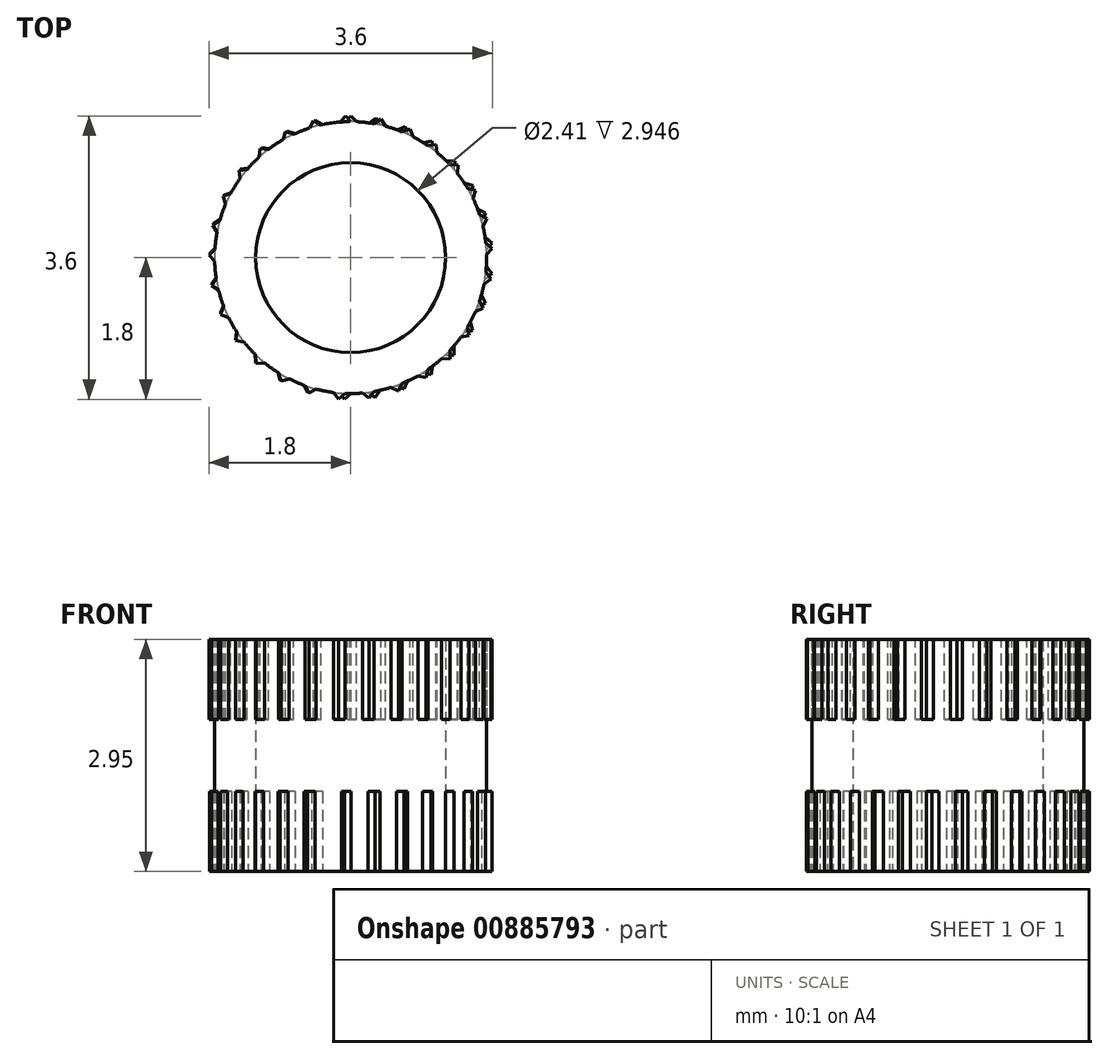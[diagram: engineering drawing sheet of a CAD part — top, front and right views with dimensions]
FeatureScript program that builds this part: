
annotation { "Feature Type Name" : "Feature", "Feature Type Description" : "" }
export const myFeature = defineFeature(function(context is Context, id is Id, definition is map)
    precondition{}
    {
        {
            var Q0;
            Q0=qCreatedBy(makeId("Top.planeOp"),FACE);
            var sketch = newSketch(context, id + "F0", { "sketchPlane" : qUnion([Q0])});
            skCircle(sketch, "E0", {"center": v(0, 0) * mm, "radius": 1.2 * mm});
            skCircle(sketch, "E1", {"center": v(0, 0) * mm, "radius": 1.73 * mm});
            skSolve(sketch);
        }
        {
            var Q0;
            Q0 = qSketchRegion(id + "F0", true);
            extrude(context, id + "F1", {"entities" : qUnion([Q0]), "depth" : 2.95 * mm, "offsetDistance" : 25.4 * mm});
        }
        {
            var Q0;
            Q0=makeQuery(id+"F1.opExtrude","CAP_FACE",FACE,{"disambiguationData":[OSD([sQuery(id+"F0.wireOp",EDGE,"E0"),sQuery(id+"F0.wireOp",EDGE,"E1")])],"isStart":false});
            var sketch = newSketch(context, id + "F2", { "sketchPlane" : qUnion([Q0])});
            skLineSegment(sketch, "E2.bottom", {"start": v(-0.24, 1.56) * mm, "end": v(-0.01, 1.33) * mm});
            skLineSegment(sketch, "E2.top", {"start": v(0, 1.8) * mm, "end": v(0.23, 1.57) * mm});
            skLineSegment(sketch, "E2.left", {"start": v(-0.24, 1.56) * mm, "end": v(0, 1.8) * mm});
            skLineSegment(sketch, "E2.right", {"start": v(-0.01, 1.33) * mm, "end": v(0.23, 1.57) * mm});
            skLineSegment(sketch, "E3.1.0", {"start": v(0.1, 1.57) * mm, "end": v(0.39, 1.76) * mm});
            skLineSegment(sketch, "E3.1.1", {"start": v(0.1, 1.57) * mm, "end": v(0.27, 1.3) * mm});
            skLineSegment(sketch, "E3.1.2", {"start": v(0.39, 1.76) * mm, "end": v(0.56, 1.49) * mm});
            skLineSegment(sketch, "E3.1.3", {"start": v(0.27, 1.3) * mm, "end": v(0.56, 1.49) * mm});
            skLineSegment(sketch, "E3.2.0", {"start": v(0.43, 1.52) * mm, "end": v(0.75, 1.64) * mm});
            skLineSegment(sketch, "E3.2.1", {"start": v(0.43, 1.52) * mm, "end": v(0.55, 1.22) * mm});
            skLineSegment(sketch, "E3.2.2", {"start": v(0.75, 1.64) * mm, "end": v(0.86, 1.34) * mm});
            skLineSegment(sketch, "E3.2.3", {"start": v(0.55, 1.22) * mm, "end": v(0.86, 1.34) * mm});
            skLineSegment(sketch, "E3.3.0", {"start": v(0.75, 1.39) * mm, "end": v(1.08, 1.44) * mm});
            skLineSegment(sketch, "E3.3.1", {"start": v(0.75, 1.39) * mm, "end": v(0.8, 1.07) * mm});
            skLineSegment(sketch, "E3.3.2", {"start": v(1.08, 1.44) * mm, "end": v(1.13, 1.12) * mm});
            skLineSegment(sketch, "E3.3.3", {"start": v(0.8, 1.07) * mm, "end": v(1.13, 1.12) * mm});
            skLineSegment(sketch, "E3.4.0", {"start": v(1.03, 1.2) * mm, "end": v(1.37, 1.17) * mm});
            skLineSegment(sketch, "E3.4.1", {"start": v(1.03, 1.2) * mm, "end": v(1, 0.88) * mm});
            skLineSegment(sketch, "E3.4.2", {"start": v(1.37, 1.17) * mm, "end": v(1.34, 0.85) * mm});
            skLineSegment(sketch, "E3.4.3", {"start": v(1, 0.88) * mm, "end": v(1.34, 0.85) * mm});
            skLineSegment(sketch, "E3.5.0", {"start": v(1.26, 0.95) * mm, "end": v(1.58, 0.85) * mm});
            skLineSegment(sketch, "E3.5.1", {"start": v(1.26, 0.95) * mm, "end": v(1.17, 0.64) * mm});
            skLineSegment(sketch, "E3.5.2", {"start": v(1.58, 0.85) * mm, "end": v(1.5, 0.55) * mm});
            skLineSegment(sketch, "E3.5.3", {"start": v(1.17, 0.64) * mm, "end": v(1.5, 0.55) * mm});
            skLineSegment(sketch, "E3.6.0", {"start": v(1.43, 0.66) * mm, "end": v(1.73, 0.5) * mm});
            skLineSegment(sketch, "E3.6.1", {"start": v(1.43, 0.66) * mm, "end": v(1.28, 0.38) * mm});
            skLineSegment(sketch, "E3.6.2", {"start": v(1.73, 0.5) * mm, "end": v(1.58, 0.22) * mm});
            skLineSegment(sketch, "E3.6.3", {"start": v(1.28, 0.38) * mm, "end": v(1.58, 0.22) * mm});
            skLineSegment(sketch, "E3.7.0", {"start": v(1.54, 0.34) * mm, "end": v(1.8, 0.12) * mm});
            skLineSegment(sketch, "E3.7.1", {"start": v(1.54, 0.34) * mm, "end": v(1.33, 0.1) * mm});
            skLineSegment(sketch, "E3.7.2", {"start": v(1.8, 0.12) * mm, "end": v(1.59, -0.12) * mm});
            skLineSegment(sketch, "E3.7.3", {"start": v(1.33, 0.1) * mm, "end": v(1.59, -0.12) * mm});
            skLineSegment(sketch, "E3.8.0", {"start": v(1.58, 0) * mm, "end": v(1.78, -0.27) * mm});
            skLineSegment(sketch, "E3.8.1", {"start": v(1.58, 0) * mm, "end": v(1.32, -0.19) * mm});
            skLineSegment(sketch, "E3.8.2", {"start": v(1.78, -0.27) * mm, "end": v(1.52, -0.46) * mm});
            skLineSegment(sketch, "E3.8.3", {"start": v(1.32, -0.19) * mm, "end": v(1.52, -0.46) * mm});
            skLineSegment(sketch, "E3.9.0", {"start": v(1.54, -0.33) * mm, "end": v(1.68, -0.64) * mm});
            skLineSegment(sketch, "E3.9.1", {"start": v(1.54, -0.33) * mm, "end": v(1.25, -0.46) * mm});
            skLineSegment(sketch, "E3.9.2", {"start": v(1.68, -0.64) * mm, "end": v(1.39, -0.77) * mm});
            skLineSegment(sketch, "E3.9.3", {"start": v(1.25, -0.46) * mm, "end": v(1.39, -0.77) * mm});
            skLineSegment(sketch, "E3.10.0", {"start": v(1.44, -0.65) * mm, "end": v(1.5, -0.99) * mm});
            skLineSegment(sketch, "E3.10.1", {"start": v(1.44, -0.65) * mm, "end": v(1.12, -0.72) * mm});
            skLineSegment(sketch, "E3.10.2", {"start": v(1.5, -0.99) * mm, "end": v(1.2, -1.05) * mm});
            skLineSegment(sketch, "E3.10.3", {"start": v(1.12, -0.72) * mm, "end": v(1.2, -1.05) * mm});
            skLineSegment(sketch, "E3.11.0", {"start": v(1.26, -0.95) * mm, "end": v(1.26, -1.29) * mm});
            skLineSegment(sketch, "E3.11.1", {"start": v(1.26, -0.95) * mm, "end": v(0.94, -0.94) * mm});
            skLineSegment(sketch, "E3.11.2", {"start": v(1.26, -1.29) * mm, "end": v(0.94, -1.28) * mm});
            skLineSegment(sketch, "E3.11.3", {"start": v(0.94, -0.94) * mm, "end": v(0.94, -1.28) * mm});
            skLineSegment(sketch, "E3.12.0", {"start": v(1.03, -1.2) * mm, "end": v(0.96, -1.52) * mm});
            skLineSegment(sketch, "E3.12.1", {"start": v(1.03, -1.2) * mm, "end": v(0.72, -1.12) * mm});
            skLineSegment(sketch, "E3.12.2", {"start": v(0.96, -1.52) * mm, "end": v(0.65, -1.45) * mm});
            skLineSegment(sketch, "E3.12.3", {"start": v(0.72, -1.12) * mm, "end": v(0.65, -1.45) * mm});
            skLineSegment(sketch, "E3.13.0", {"start": v(0.75, -1.39) * mm, "end": v(0.61, -1.7) * mm});
            skLineSegment(sketch, "E3.13.1", {"start": v(0.75, -1.39) * mm, "end": v(0.46, -1.25) * mm});
            skLineSegment(sketch, "E3.13.2", {"start": v(0.61, -1.7) * mm, "end": v(0.32, -1.56) * mm});
            skLineSegment(sketch, "E3.13.3", {"start": v(0.46, -1.25) * mm, "end": v(0.32, -1.56) * mm});
            skLineSegment(sketch, "E3.14.0", {"start": v(0.44, -1.51) * mm, "end": v(0.23, -1.79) * mm});
            skLineSegment(sketch, "E3.14.1", {"start": v(0.44, -1.51) * mm, "end": v(0.19, -1.32) * mm});
            skLineSegment(sketch, "E3.14.2", {"start": v(0.23, -1.79) * mm, "end": v(-0.02, -1.6) * mm});
            skLineSegment(sketch, "E3.14.3", {"start": v(0.19, -1.32) * mm, "end": v(-0.02, -1.6) * mm});
            skLineSegment(sketch, "E3.15.0", {"start": v(0.1, -1.57) * mm, "end": v(-0.15, -1.8) * mm});
            skLineSegment(sketch, "E3.15.1", {"start": v(0.1, -1.57) * mm, "end": v(-0.1, -1.33) * mm});
            skLineSegment(sketch, "E3.15.2", {"start": v(-0.15, -1.8) * mm, "end": v(-0.36, -1.55) * mm});
            skLineSegment(sketch, "E3.15.3", {"start": v(-0.1, -1.33) * mm, "end": v(-0.36, -1.55) * mm});
            skLineSegment(sketch, "E3.16.0", {"start": v(-0.23, -1.56) * mm, "end": v(-0.53, -1.72) * mm});
            skLineSegment(sketch, "E3.16.1", {"start": v(-0.23, -1.56) * mm, "end": v(-0.38, -1.28) * mm});
            skLineSegment(sketch, "E3.16.2", {"start": v(-0.53, -1.72) * mm, "end": v(-0.68, -1.44) * mm});
            skLineSegment(sketch, "E3.16.3", {"start": v(-0.38, -1.28) * mm, "end": v(-0.68, -1.44) * mm});
            skLineSegment(sketch, "E3.17.0", {"start": v(-0.56, -1.48) * mm, "end": v(-0.89, -1.57) * mm});
            skLineSegment(sketch, "E3.17.1", {"start": v(-0.56, -1.48) * mm, "end": v(-0.64, -1.17) * mm});
            skLineSegment(sketch, "E3.17.2", {"start": v(-0.89, -1.57) * mm, "end": v(-0.97, -1.26) * mm});
            skLineSegment(sketch, "E3.17.3", {"start": v(-0.64, -1.17) * mm, "end": v(-0.97, -1.26) * mm});
            skLineSegment(sketch, "E3.18.0", {"start": v(-0.86, -1.32) * mm, "end": v(-1.2, -1.34) * mm});
            skLineSegment(sketch, "E3.18.1", {"start": v(-0.86, -1.32) * mm, "end": v(-0.88, -1) * mm});
            skLineSegment(sketch, "E3.18.2", {"start": v(-1.2, -1.34) * mm, "end": v(-1.22, -1.02) * mm});
            skLineSegment(sketch, "E3.18.3", {"start": v(-0.88, -1) * mm, "end": v(-1.22, -1.02) * mm});
            skLineSegment(sketch, "E3.19.0", {"start": v(-1.12, -1.1) * mm, "end": v(-1.46, -1.06) * mm});
            skLineSegment(sketch, "E3.19.1", {"start": v(-1.12, -1.1) * mm, "end": v(-1.07, -0.8) * mm});
            skLineSegment(sketch, "E3.19.2", {"start": v(-1.46, -1.06) * mm, "end": v(-1.4, -0.74) * mm});
            skLineSegment(sketch, "E3.19.3", {"start": v(-1.07, -0.8) * mm, "end": v(-1.4, -0.74) * mm});
            skLineSegment(sketch, "E3.20.0", {"start": v(-1.33, -0.84) * mm, "end": v(-1.65, -0.72) * mm});
            skLineSegment(sketch, "E3.20.1", {"start": v(-1.33, -0.84) * mm, "end": v(-1.22, -0.55) * mm});
            skLineSegment(sketch, "E3.20.2", {"start": v(-1.65, -0.72) * mm, "end": v(-1.53, -0.42) * mm});
            skLineSegment(sketch, "E3.20.3", {"start": v(-1.22, -0.55) * mm, "end": v(-1.53, -0.42) * mm});
            skLineSegment(sketch, "E3.21.0", {"start": v(-1.48, -0.54) * mm, "end": v(-1.77, -0.35) * mm});
            skLineSegment(sketch, "E3.21.1", {"start": v(-1.48, -0.54) * mm, "end": v(-1.3, -0.27) * mm});
            skLineSegment(sketch, "E3.21.2", {"start": v(-1.77, -0.35) * mm, "end": v(-1.59, -0.09) * mm});
            skLineSegment(sketch, "E3.21.3", {"start": v(-1.3, -0.27) * mm, "end": v(-1.59, -0.09) * mm});
            skLineSegment(sketch, "E3.22.0", {"start": v(-1.56, -0.21) * mm, "end": v(-1.8, 0.03) * mm});
            skLineSegment(sketch, "E3.22.1", {"start": v(-1.56, -0.21) * mm, "end": v(-1.33, 0.01) * mm});
            skLineSegment(sketch, "E3.22.2", {"start": v(-1.8, 0.03) * mm, "end": v(-1.57, 0.25) * mm});
            skLineSegment(sketch, "E3.22.3", {"start": v(-1.33, 0.01) * mm, "end": v(-1.57, 0.25) * mm});
            skLineSegment(sketch, "E3.23.0", {"start": v(-1.57, 0.13) * mm, "end": v(-1.75, 0.42) * mm});
            skLineSegment(sketch, "E3.23.1", {"start": v(-1.57, 0.13) * mm, "end": v(-1.3, 0.3) * mm});
            skLineSegment(sketch, "E3.23.2", {"start": v(-1.75, 0.42) * mm, "end": v(-1.48, 0.58) * mm});
            skLineSegment(sketch, "E3.23.3", {"start": v(-1.3, 0.3) * mm, "end": v(-1.48, 0.58) * mm});
            skLineSegment(sketch, "E3.24.0", {"start": v(-1.5, 0.46) * mm, "end": v(-1.62, 0.78) * mm});
            skLineSegment(sketch, "E3.24.1", {"start": v(-1.5, 0.46) * mm, "end": v(-1.2, 0.56) * mm});
            skLineSegment(sketch, "E3.24.2", {"start": v(-1.62, 0.78) * mm, "end": v(-1.32, 0.89) * mm});
            skLineSegment(sketch, "E3.24.3", {"start": v(-1.2, 0.56) * mm, "end": v(-1.32, 0.89) * mm});
            skLineSegment(sketch, "E3.25.0", {"start": v(-1.38, 0.77) * mm, "end": v(-1.42, 1.1) * mm});
            skLineSegment(sketch, "E3.25.1", {"start": v(-1.38, 0.77) * mm, "end": v(-1.06, 0.8) * mm});
            skLineSegment(sketch, "E3.25.2", {"start": v(-1.42, 1.1) * mm, "end": v(-1.1, 1.15) * mm});
            skLineSegment(sketch, "E3.25.3", {"start": v(-1.06, 0.8) * mm, "end": v(-1.1, 1.15) * mm});
            skLineSegment(sketch, "E3.26.0", {"start": v(-1.18, 1.05) * mm, "end": v(-1.15, 1.38) * mm});
            skLineSegment(sketch, "E3.26.1", {"start": v(-1.18, 1.05) * mm, "end": v(-0.86, 1.02) * mm});
            skLineSegment(sketch, "E3.26.2", {"start": v(-1.15, 1.38) * mm, "end": v(-0.83, 1.36) * mm});
            skLineSegment(sketch, "E3.26.3", {"start": v(-0.86, 1.02) * mm, "end": v(-0.83, 1.36) * mm});
            skLineSegment(sketch, "E3.27.0", {"start": v(-0.93, 1.27) * mm, "end": v(-0.83, 1.6) * mm});
            skLineSegment(sketch, "E3.27.1", {"start": v(-0.93, 1.27) * mm, "end": v(-0.63, 1.18) * mm});
            skLineSegment(sketch, "E3.27.2", {"start": v(-0.83, 1.6) * mm, "end": v(-0.52, 1.5) * mm});
            skLineSegment(sketch, "E3.27.3", {"start": v(-0.63, 1.18) * mm, "end": v(-0.52, 1.5) * mm});
            skLineSegment(sketch, "E3.28.0", {"start": v(-0.64, 1.44) * mm, "end": v(-0.47, 1.74) * mm});
            skLineSegment(sketch, "E3.28.1", {"start": v(-0.64, 1.44) * mm, "end": v(-0.36, 1.28) * mm});
            skLineSegment(sketch, "E3.28.2", {"start": v(-0.47, 1.74) * mm, "end": v(-0.2, 1.58) * mm});
            skLineSegment(sketch, "E3.28.3", {"start": v(-0.36, 1.28) * mm, "end": v(-0.2, 1.58) * mm});
            skLineSegment(sketch, "E3.29.0", {"start": v(-0.32, 1.55) * mm, "end": v(-0.09, 1.8) * mm});
            skLineSegment(sketch, "E3.29.1", {"start": v(-0.32, 1.55) * mm, "end": v(-0.08, 1.33) * mm});
            skLineSegment(sketch, "E3.29.2", {"start": v(-0.09, 1.8) * mm, "end": v(0.15, 1.58) * mm});
            skLineSegment(sketch, "E3.29.3", {"start": v(-0.08, 1.33) * mm, "end": v(0.15, 1.58) * mm});
            skPoint(sketch, "E3.center", {"position": v(0, 0) * mm});
            skLineSegment(sketch, "E3.anchor1", {"start": v(0, 0) * mm, "end": v(-0.01, 1.33) * mm, "construction": true});
            skLineSegment(sketch, "E3.anchor2", {"start": v(0, 0) * mm, "end": v(-0.08, 1.33) * mm, "construction": true});
            skSolve(sketch);
        }
        {
            var Q0;
            {var subQ0=sQuery(id+"F2.wireOp",EDGE,"E3.25.2");var subQ1=sQuery(id+"F2.wireOp",EDGE,"E3.25.0");var subQ2=makeQuery(id+"F2.imprint","INTERSECT",VERTEX,{"derivedFrom":[subQ1,subQ0]});Q0=makeQuery(id+"F2.imprint","IMPRINT",FACE,{"disambiguationData":[TD([[makeQuery(id+"F2.imprint","IMPRINT",EDGE,{"disambiguationData":[TD([[subQ2,1.0]])],"derivedFrom":subQ1}),-1.0]])]});}
            var Q1;
            {var subQ0=sQuery(id+"F2.wireOp",EDGE,"E3.26.2");var subQ1=sQuery(id+"F2.wireOp",EDGE,"E3.26.0");var subQ2=makeQuery(id+"F2.imprint","INTERSECT",VERTEX,{"derivedFrom":[subQ1,subQ0]});Q1=makeQuery(id+"F2.imprint","IMPRINT",FACE,{"disambiguationData":[TD([[makeQuery(id+"F2.imprint","IMPRINT",EDGE,{"disambiguationData":[TD([[subQ2,1.0]])],"derivedFrom":subQ1}),-1.0]])]});}
            var Q2;
            {var subQ0=sQuery(id+"F2.wireOp",EDGE,"E3.27.2");var subQ1=sQuery(id+"F2.wireOp",EDGE,"E3.27.0");var subQ2=makeQuery(id+"F2.imprint","INTERSECT",VERTEX,{"derivedFrom":[subQ1,subQ0]});Q2=makeQuery(id+"F2.imprint","IMPRINT",FACE,{"disambiguationData":[TD([[makeQuery(id+"F2.imprint","IMPRINT",EDGE,{"disambiguationData":[TD([[subQ2,1.0]])],"derivedFrom":subQ1}),-1.0]])]});}
            var Q3;
            {var subQ0=sQuery(id+"F2.wireOp",EDGE,"E3.28.2");var subQ1=sQuery(id+"F2.wireOp",EDGE,"E3.28.0");var subQ2=makeQuery(id+"F2.imprint","INTERSECT",VERTEX,{"derivedFrom":[subQ1,subQ0]});Q3=makeQuery(id+"F2.imprint","IMPRINT",FACE,{"disambiguationData":[TD([[makeQuery(id+"F2.imprint","IMPRINT",EDGE,{"disambiguationData":[TD([[subQ2,1.0]])],"derivedFrom":subQ1}),-1.0]])]});}
            var Q4;
            {var subQ0=sQuery(id+"F2.wireOp",EDGE,"E2.left");var subQ1=sQuery(id+"F2.wireOp",EDGE,"E2.top");var subQ2=makeQuery(id+"F2.imprint","INTERSECT",VERTEX,{"derivedFrom":[subQ1,subQ0]});Q4=makeQuery(id+"F2.imprint","IMPRINT",FACE,{"disambiguationData":[TD([[makeQuery(id+"F2.imprint","IMPRINT",EDGE,{"disambiguationData":[TD([[subQ2,-1.0]])],"derivedFrom":subQ1}),-1.0]])]});}
            var Q5;
            {var subQ0=sQuery(id+"F2.wireOp",EDGE,"E3.1.2");var subQ1=sQuery(id+"F2.wireOp",EDGE,"E3.1.0");var subQ2=makeQuery(id+"F2.imprint","INTERSECT",VERTEX,{"derivedFrom":[subQ1,subQ0]});Q5=makeQuery(id+"F2.imprint","IMPRINT",FACE,{"disambiguationData":[TD([[makeQuery(id+"F2.imprint","IMPRINT",EDGE,{"disambiguationData":[TD([[subQ2,1.0]])],"derivedFrom":subQ1}),-1.0]])]});}
            var Q6;
            {var subQ0=sQuery(id+"F2.wireOp",EDGE,"E3.2.2");var subQ1=sQuery(id+"F2.wireOp",EDGE,"E3.2.0");var subQ2=makeQuery(id+"F2.imprint","INTERSECT",VERTEX,{"derivedFrom":[subQ1,subQ0]});Q6=makeQuery(id+"F2.imprint","IMPRINT",FACE,{"disambiguationData":[TD([[makeQuery(id+"F2.imprint","IMPRINT",EDGE,{"disambiguationData":[TD([[subQ2,1.0]])],"derivedFrom":subQ1}),-1.0]])]});}
            var Q7;
            {var subQ0=sQuery(id+"F2.wireOp",EDGE,"E3.4.2");var subQ1=sQuery(id+"F2.wireOp",EDGE,"E3.4.0");var subQ2=makeQuery(id+"F2.imprint","INTERSECT",VERTEX,{"derivedFrom":[subQ1,subQ0]});Q7=makeQuery(id+"F2.imprint","IMPRINT",FACE,{"disambiguationData":[TD([[makeQuery(id+"F2.imprint","IMPRINT",EDGE,{"disambiguationData":[TD([[subQ2,1.0]])],"derivedFrom":subQ1}),-1.0]])]});}
            var Q8;
            {var subQ0=sQuery(id+"F2.wireOp",EDGE,"E3.5.2");var subQ1=sQuery(id+"F2.wireOp",EDGE,"E3.5.0");var subQ2=makeQuery(id+"F2.imprint","INTERSECT",VERTEX,{"derivedFrom":[subQ1,subQ0]});Q8=makeQuery(id+"F2.imprint","IMPRINT",FACE,{"disambiguationData":[TD([[makeQuery(id+"F2.imprint","IMPRINT",EDGE,{"disambiguationData":[TD([[subQ2,1.0]])],"derivedFrom":subQ1}),-1.0]])]});}
            var Q9;
            {var subQ0=sQuery(id+"F2.wireOp",EDGE,"E3.6.2");var subQ1=sQuery(id+"F2.wireOp",EDGE,"E3.6.0");var subQ2=makeQuery(id+"F2.imprint","INTERSECT",VERTEX,{"derivedFrom":[subQ1,subQ0]});Q9=makeQuery(id+"F2.imprint","IMPRINT",FACE,{"disambiguationData":[TD([[makeQuery(id+"F2.imprint","IMPRINT",EDGE,{"disambiguationData":[TD([[subQ2,1.0]])],"derivedFrom":subQ1}),-1.0]])]});}
            var Q10;
            {var subQ0=sQuery(id+"F2.wireOp",EDGE,"E3.7.2");var subQ1=sQuery(id+"F2.wireOp",EDGE,"E3.7.0");var subQ2=makeQuery(id+"F2.imprint","INTERSECT",VERTEX,{"derivedFrom":[subQ1,subQ0]});Q10=makeQuery(id+"F2.imprint","IMPRINT",FACE,{"disambiguationData":[TD([[makeQuery(id+"F2.imprint","IMPRINT",EDGE,{"disambiguationData":[TD([[subQ2,1.0]])],"derivedFrom":subQ1}),-1.0]])]});}
            var Q11;
            {var subQ0=sQuery(id+"F2.wireOp",EDGE,"E3.8.2");var subQ1=sQuery(id+"F2.wireOp",EDGE,"E3.8.0");var subQ2=makeQuery(id+"F2.imprint","INTERSECT",VERTEX,{"derivedFrom":[subQ1,subQ0]});Q11=makeQuery(id+"F2.imprint","IMPRINT",FACE,{"disambiguationData":[TD([[makeQuery(id+"F2.imprint","IMPRINT",EDGE,{"disambiguationData":[TD([[subQ2,1.0]])],"derivedFrom":subQ1}),-1.0]])]});}
            var Q12;
            {var subQ0=sQuery(id+"F2.wireOp",EDGE,"E3.23.2");var subQ1=sQuery(id+"F2.wireOp",EDGE,"E3.23.0");var subQ2=makeQuery(id+"F2.imprint","INTERSECT",VERTEX,{"derivedFrom":[subQ1,subQ0]});Q12=makeQuery(id+"F2.imprint","IMPRINT",FACE,{"disambiguationData":[TD([[makeQuery(id+"F2.imprint","IMPRINT",EDGE,{"disambiguationData":[TD([[subQ2,1.0]])],"derivedFrom":subQ1}),-1.0]])]});}
            var Q13;
            {var subQ0=sQuery(id+"F2.wireOp",EDGE,"E3.21.2");var subQ1=sQuery(id+"F2.wireOp",EDGE,"E3.21.0");var subQ2=makeQuery(id+"F2.imprint","INTERSECT",VERTEX,{"derivedFrom":[subQ1,subQ0]});Q13=makeQuery(id+"F2.imprint","IMPRINT",FACE,{"disambiguationData":[TD([[makeQuery(id+"F2.imprint","IMPRINT",EDGE,{"disambiguationData":[TD([[subQ2,1.0]])],"derivedFrom":subQ1}),-1.0]])]});}
            var Q14;
            {var subQ0=sQuery(id+"F2.wireOp",EDGE,"E3.20.2");var subQ1=sQuery(id+"F2.wireOp",EDGE,"E3.20.0");var subQ2=makeQuery(id+"F2.imprint","INTERSECT",VERTEX,{"derivedFrom":[subQ1,subQ0]});Q14=makeQuery(id+"F2.imprint","IMPRINT",FACE,{"disambiguationData":[TD([[makeQuery(id+"F2.imprint","IMPRINT",EDGE,{"disambiguationData":[TD([[subQ2,1.0]])],"derivedFrom":subQ1}),-1.0]])]});}
            var Q15;
            {var subQ0=sQuery(id+"F2.wireOp",EDGE,"E3.19.2");var subQ1=sQuery(id+"F2.wireOp",EDGE,"E3.19.0");var subQ2=makeQuery(id+"F2.imprint","INTERSECT",VERTEX,{"derivedFrom":[subQ1,subQ0]});Q15=makeQuery(id+"F2.imprint","IMPRINT",FACE,{"disambiguationData":[TD([[makeQuery(id+"F2.imprint","IMPRINT",EDGE,{"disambiguationData":[TD([[subQ2,1.0]])],"derivedFrom":subQ1}),-1.0]])]});}
            var Q16;
            {var subQ0=sQuery(id+"F2.wireOp",EDGE,"E3.18.2");var subQ1=sQuery(id+"F2.wireOp",EDGE,"E3.18.0");var subQ2=makeQuery(id+"F2.imprint","INTERSECT",VERTEX,{"derivedFrom":[subQ1,subQ0]});Q16=makeQuery(id+"F2.imprint","IMPRINT",FACE,{"disambiguationData":[TD([[makeQuery(id+"F2.imprint","IMPRINT",EDGE,{"disambiguationData":[TD([[subQ2,1.0]])],"derivedFrom":subQ1}),-1.0]])]});}
            var Q17;
            {var subQ0=sQuery(id+"F2.wireOp",EDGE,"E3.17.2");var subQ1=sQuery(id+"F2.wireOp",EDGE,"E3.17.0");var subQ2=makeQuery(id+"F2.imprint","INTERSECT",VERTEX,{"derivedFrom":[subQ1,subQ0]});Q17=makeQuery(id+"F2.imprint","IMPRINT",FACE,{"disambiguationData":[TD([[makeQuery(id+"F2.imprint","IMPRINT",EDGE,{"disambiguationData":[TD([[subQ2,1.0]])],"derivedFrom":subQ1}),-1.0]])]});}
            var Q18;
            {var subQ0=sQuery(id+"F2.wireOp",EDGE,"E3.16.2");var subQ1=sQuery(id+"F2.wireOp",EDGE,"E3.16.0");var subQ2=makeQuery(id+"F2.imprint","INTERSECT",VERTEX,{"derivedFrom":[subQ1,subQ0]});Q18=makeQuery(id+"F2.imprint","IMPRINT",FACE,{"disambiguationData":[TD([[makeQuery(id+"F2.imprint","IMPRINT",EDGE,{"disambiguationData":[TD([[subQ2,1.0]])],"derivedFrom":subQ1}),-1.0]])]});}
            var Q19;
            {var subQ0=sQuery(id+"F2.wireOp",EDGE,"E3.15.2");var subQ1=sQuery(id+"F2.wireOp",EDGE,"E3.15.0");var subQ2=makeQuery(id+"F2.imprint","INTERSECT",VERTEX,{"derivedFrom":[subQ1,subQ0]});Q19=makeQuery(id+"F2.imprint","IMPRINT",FACE,{"disambiguationData":[TD([[makeQuery(id+"F2.imprint","IMPRINT",EDGE,{"disambiguationData":[TD([[subQ2,1.0]])],"derivedFrom":subQ1}),-1.0]])]});}
            var Q20;
            {var subQ0=sQuery(id+"F2.wireOp",EDGE,"E3.14.2");var subQ1=sQuery(id+"F2.wireOp",EDGE,"E3.14.0");var subQ2=makeQuery(id+"F2.imprint","INTERSECT",VERTEX,{"derivedFrom":[subQ1,subQ0]});Q20=makeQuery(id+"F2.imprint","IMPRINT",FACE,{"disambiguationData":[TD([[makeQuery(id+"F2.imprint","IMPRINT",EDGE,{"disambiguationData":[TD([[subQ2,1.0]])],"derivedFrom":subQ1}),-1.0]])]});}
            var Q21;
            {var subQ0=sQuery(id+"F2.wireOp",EDGE,"E3.13.2");var subQ1=sQuery(id+"F2.wireOp",EDGE,"E3.13.0");var subQ2=makeQuery(id+"F2.imprint","INTERSECT",VERTEX,{"derivedFrom":[subQ1,subQ0]});Q21=makeQuery(id+"F2.imprint","IMPRINT",FACE,{"disambiguationData":[TD([[makeQuery(id+"F2.imprint","IMPRINT",EDGE,{"disambiguationData":[TD([[subQ2,1.0]])],"derivedFrom":subQ1}),-1.0]])]});}
            var Q22;
            {var subQ0=sQuery(id+"F2.wireOp",EDGE,"E3.12.2");var subQ1=sQuery(id+"F2.wireOp",EDGE,"E3.12.0");var subQ2=makeQuery(id+"F2.imprint","INTERSECT",VERTEX,{"derivedFrom":[subQ1,subQ0]});Q22=makeQuery(id+"F2.imprint","IMPRINT",FACE,{"disambiguationData":[TD([[makeQuery(id+"F2.imprint","IMPRINT",EDGE,{"disambiguationData":[TD([[subQ2,1.0]])],"derivedFrom":subQ1}),-1.0]])]});}
            var Q23;
            {var subQ0=sQuery(id+"F2.wireOp",EDGE,"E3.11.2");var subQ1=sQuery(id+"F2.wireOp",EDGE,"E3.11.0");var subQ2=makeQuery(id+"F2.imprint","INTERSECT",VERTEX,{"derivedFrom":[subQ1,subQ0]});Q23=makeQuery(id+"F2.imprint","IMPRINT",FACE,{"disambiguationData":[TD([[makeQuery(id+"F2.imprint","IMPRINT",EDGE,{"disambiguationData":[TD([[subQ2,1.0]])],"derivedFrom":subQ1}),-1.0]])]});}
            var Q24;
            {var subQ0=sQuery(id+"F2.wireOp",EDGE,"E3.10.2");var subQ1=sQuery(id+"F2.wireOp",EDGE,"E3.10.0");var subQ2=makeQuery(id+"F2.imprint","INTERSECT",VERTEX,{"derivedFrom":[subQ1,subQ0]});Q24=makeQuery(id+"F2.imprint","IMPRINT",FACE,{"disambiguationData":[TD([[makeQuery(id+"F2.imprint","IMPRINT",EDGE,{"disambiguationData":[TD([[subQ2,1.0]])],"derivedFrom":subQ1}),-1.0]])]});}
            var Q25;
            {var subQ0=sQuery(id+"F2.wireOp",EDGE,"E3.9.2");var subQ1=sQuery(id+"F2.wireOp",EDGE,"E3.9.0");var subQ2=makeQuery(id+"F2.imprint","INTERSECT",VERTEX,{"derivedFrom":[subQ1,subQ0]});Q25=makeQuery(id+"F2.imprint","IMPRINT",FACE,{"disambiguationData":[TD([[makeQuery(id+"F2.imprint","IMPRINT",EDGE,{"disambiguationData":[TD([[subQ2,1.0]])],"derivedFrom":subQ1}),-1.0]])]});}
            var Q26;
            {var subQ0=sQuery(id+"F2.wireOp",EDGE,"E3.3.2");var subQ1=sQuery(id+"F2.wireOp",EDGE,"E3.3.0");var subQ2=makeQuery(id+"F2.imprint","INTERSECT",VERTEX,{"derivedFrom":[subQ1,subQ0]});Q26=makeQuery(id+"F2.imprint","IMPRINT",FACE,{"disambiguationData":[TD([[makeQuery(id+"F2.imprint","IMPRINT",EDGE,{"disambiguationData":[TD([[subQ2,1.0]])],"derivedFrom":subQ1}),-1.0]])]});}
            var Q27;
            {var subQ0=sQuery(id+"F2.wireOp",EDGE,"E3.24.2");var subQ1=sQuery(id+"F2.wireOp",EDGE,"E3.24.0");var subQ2=makeQuery(id+"F2.imprint","INTERSECT",VERTEX,{"derivedFrom":[subQ1,subQ0]});Q27=makeQuery(id+"F2.imprint","IMPRINT",FACE,{"disambiguationData":[TD([[makeQuery(id+"F2.imprint","IMPRINT",EDGE,{"disambiguationData":[TD([[subQ2,1.0]])],"derivedFrom":subQ1}),-1.0]])]});}
            var Q28;
            {var subQ0=sQuery(id+"F2.wireOp",EDGE,"E3.22.2");var subQ1=sQuery(id+"F2.wireOp",EDGE,"E3.22.0");var subQ2=makeQuery(id+"F2.imprint","INTERSECT",VERTEX,{"derivedFrom":[subQ1,subQ0]});Q28=makeQuery(id+"F2.imprint","IMPRINT",FACE,{"disambiguationData":[TD([[makeQuery(id+"F2.imprint","IMPRINT",EDGE,{"disambiguationData":[TD([[subQ2,1.0]])],"derivedFrom":subQ1}),-1.0]])]});}
            extrude(context, id + "F3", {"entities" : qUnion([Q0, Q1, Q2, Q3, Q4, Q5, Q6, Q7, Q8, Q9, Q10, Q11, Q12, Q13, Q14, Q15, Q16, Q17, Q18, Q19, Q20, Q21, Q22, Q23, Q24, Q25, Q26, Q27, Q28]), "operationType" : NewBodyOperationType.ADD, "oppositeDirection" : true, "depth" : 1.02 * mm, "offsetDistance" : 25.4 * mm});
        }
        {
            var Q0;
            Q0=makeQuery(id+"F1.opExtrude","CAP_FACE",FACE,{"disambiguationData":[OSD([sQuery(id+"F0.wireOp",EDGE,"E0"),sQuery(id+"F0.wireOp",EDGE,"E1")])],"isStart":true});
            var sketch = newSketch(context, id + "F4", { "sketchPlane" : qUnion([Q0])});
            skLineSegment(sketch, "E4.bottom", {"start": v(-0.3, 1.55) * mm, "end": v(-0.07, 1.33) * mm});
            skLineSegment(sketch, "E4.top", {"start": v(-0.08, 1.8) * mm, "end": v(0.16, 1.58) * mm});
            skLineSegment(sketch, "E4.left", {"start": v(-0.3, 1.55) * mm, "end": v(-0.08, 1.8) * mm});
            skLineSegment(sketch, "E4.right", {"start": v(-0.07, 1.33) * mm, "end": v(0.16, 1.58) * mm});
            skLineSegment(sketch, "E5.1.0", {"start": v(0.03, 1.58) * mm, "end": v(0.3, 1.77) * mm});
            skLineSegment(sketch, "E5.1.1", {"start": v(0.03, 1.58) * mm, "end": v(0.22, 1.32) * mm});
            skLineSegment(sketch, "E5.1.2", {"start": v(0.3, 1.77) * mm, "end": v(0.5, 1.51) * mm});
            skLineSegment(sketch, "E5.1.3", {"start": v(0.22, 1.32) * mm, "end": v(0.5, 1.51) * mm});
            skLineSegment(sketch, "E5.2.0", {"start": v(0.37, 1.54) * mm, "end": v(0.68, 1.67) * mm});
            skLineSegment(sketch, "E5.2.1", {"start": v(0.37, 1.54) * mm, "end": v(0.5, 1.24) * mm});
            skLineSegment(sketch, "E5.2.2", {"start": v(0.68, 1.67) * mm, "end": v(0.8, 1.37) * mm});
            skLineSegment(sketch, "E5.2.3", {"start": v(0.5, 1.24) * mm, "end": v(0.8, 1.37) * mm});
            skLineSegment(sketch, "E5.3.0", {"start": v(0.69, 1.42) * mm, "end": v(1.02, 1.49) * mm});
            skLineSegment(sketch, "E5.3.1", {"start": v(0.69, 1.42) * mm, "end": v(0.75, 1.1) * mm});
            skLineSegment(sketch, "E5.3.2", {"start": v(1.02, 1.49) * mm, "end": v(1.08, 1.17) * mm});
            skLineSegment(sketch, "E5.3.3", {"start": v(0.75, 1.1) * mm, "end": v(1.08, 1.17) * mm});
            skLineSegment(sketch, "E5.4.0", {"start": v(0.97, 1.24) * mm, "end": v(1.32, 1.24) * mm});
            skLineSegment(sketch, "E5.4.1", {"start": v(0.97, 1.24) * mm, "end": v(0.97, 0.92) * mm});
            skLineSegment(sketch, "E5.4.2", {"start": v(1.32, 1.24) * mm, "end": v(1.3, 0.92) * mm});
            skLineSegment(sketch, "E5.4.3", {"start": v(0.97, 0.92) * mm, "end": v(1.3, 0.92) * mm});
            skLineSegment(sketch, "E5.5.0", {"start": v(1.22, 1) * mm, "end": v(1.55, 0.93) * mm});
            skLineSegment(sketch, "E5.5.1", {"start": v(1.22, 1) * mm, "end": v(1.14, 0.7) * mm});
            skLineSegment(sketch, "E5.5.2", {"start": v(1.55, 0.93) * mm, "end": v(1.47, 0.62) * mm});
            skLineSegment(sketch, "E5.5.3", {"start": v(1.14, 0.7) * mm, "end": v(1.47, 0.62) * mm});
            skLineSegment(sketch, "E5.6.0", {"start": v(1.4, 0.73) * mm, "end": v(1.71, 0.58) * mm});
            skLineSegment(sketch, "E5.6.1", {"start": v(1.4, 0.73) * mm, "end": v(1.26, 0.44) * mm});
            skLineSegment(sketch, "E5.6.2", {"start": v(1.71, 0.58) * mm, "end": v(1.57, 0.3) * mm});
            skLineSegment(sketch, "E5.6.3", {"start": v(1.26, 0.44) * mm, "end": v(1.57, 0.3) * mm});
            skLineSegment(sketch, "E5.7.0", {"start": v(1.53, 0.41) * mm, "end": v(1.8, 0.2) * mm});
            skLineSegment(sketch, "E5.7.1", {"start": v(1.53, 0.41) * mm, "end": v(1.33, 0.16) * mm});
            skLineSegment(sketch, "E5.7.2", {"start": v(1.8, 0.2) * mm, "end": v(1.6, -0.05) * mm});
            skLineSegment(sketch, "E5.7.3", {"start": v(1.33, 0.16) * mm, "end": v(1.6, -0.05) * mm});
            skLineSegment(sketch, "E5.8.0", {"start": v(1.58, 0.08) * mm, "end": v(1.8, -0.19) * mm});
            skLineSegment(sketch, "E5.8.1", {"start": v(1.58, 0.08) * mm, "end": v(1.33, -0.12) * mm});
            skLineSegment(sketch, "E5.8.2", {"start": v(1.8, -0.19) * mm, "end": v(1.55, -0.39) * mm});
            skLineSegment(sketch, "E5.8.3", {"start": v(1.33, -0.12) * mm, "end": v(1.55, -0.39) * mm});
            skLineSegment(sketch, "E5.9.0", {"start": v(1.56, -0.26) * mm, "end": v(1.72, -0.56) * mm});
            skLineSegment(sketch, "E5.9.1", {"start": v(1.56, -0.26) * mm, "end": v(1.28, -0.4) * mm});
            skLineSegment(sketch, "E5.9.2", {"start": v(1.72, -0.56) * mm, "end": v(1.43, -0.7) * mm});
            skLineSegment(sketch, "E5.9.3", {"start": v(1.28, -0.4) * mm, "end": v(1.43, -0.7) * mm});
            skLineSegment(sketch, "E5.10.0", {"start": v(1.47, -0.59) * mm, "end": v(1.56, -0.92) * mm});
            skLineSegment(sketch, "E5.10.1", {"start": v(1.47, -0.59) * mm, "end": v(1.16, -0.67) * mm});
            skLineSegment(sketch, "E5.10.2", {"start": v(1.56, -0.92) * mm, "end": v(1.25, -1) * mm});
            skLineSegment(sketch, "E5.10.3", {"start": v(1.16, -0.67) * mm, "end": v(1.25, -1) * mm});
            skLineSegment(sketch, "E5.11.0", {"start": v(1.31, -0.88) * mm, "end": v(1.32, -1.23) * mm});
            skLineSegment(sketch, "E5.11.1", {"start": v(1.31, -0.88) * mm, "end": v(1, -0.9) * mm});
            skLineSegment(sketch, "E5.11.2", {"start": v(1.32, -1.23) * mm, "end": v(1, -1.24) * mm});
            skLineSegment(sketch, "E5.11.3", {"start": v(1, -0.9) * mm, "end": v(1, -1.24) * mm});
            skLineSegment(sketch, "E5.12.0", {"start": v(1.1, -1.14) * mm, "end": v(1.03, -1.48) * mm});
            skLineSegment(sketch, "E5.12.1", {"start": v(1.1, -1.14) * mm, "end": v(0.78, -1.09) * mm});
            skLineSegment(sketch, "E5.12.2", {"start": v(1.03, -1.48) * mm, "end": v(0.72, -1.42) * mm});
            skLineSegment(sketch, "E5.12.3", {"start": v(0.78, -1.09) * mm, "end": v(0.72, -1.42) * mm});
            skLineSegment(sketch, "E5.13.0", {"start": v(0.82, -1.35) * mm, "end": v(0.7, -1.66) * mm});
            skLineSegment(sketch, "E5.13.1", {"start": v(0.82, -1.35) * mm, "end": v(0.53, -1.23) * mm});
            skLineSegment(sketch, "E5.13.2", {"start": v(0.7, -1.66) * mm, "end": v(0.4, -1.54) * mm});
            skLineSegment(sketch, "E5.13.3", {"start": v(0.53, -1.23) * mm, "end": v(0.4, -1.54) * mm});
            skLineSegment(sketch, "E5.14.0", {"start": v(0.52, -1.5) * mm, "end": v(0.32, -1.77) * mm});
            skLineSegment(sketch, "E5.14.1", {"start": v(0.52, -1.5) * mm, "end": v(0.25, -1.3) * mm});
            skLineSegment(sketch, "E5.14.2", {"start": v(0.32, -1.77) * mm, "end": v(0.06, -1.59) * mm});
            skLineSegment(sketch, "E5.14.3", {"start": v(0.25, -1.3) * mm, "end": v(0.06, -1.59) * mm});
            skLineSegment(sketch, "E5.15.0", {"start": v(0.19, -1.57) * mm, "end": v(-0.06, -1.8) * mm});
            skLineSegment(sketch, "E5.15.1", {"start": v(0.19, -1.57) * mm, "end": v(-0.03, -1.33) * mm});
            skLineSegment(sketch, "E5.15.2", {"start": v(-0.06, -1.8) * mm, "end": v(-0.28, -1.56) * mm});
            skLineSegment(sketch, "E5.15.3", {"start": v(-0.03, -1.33) * mm, "end": v(-0.28, -1.56) * mm});
            skLineSegment(sketch, "E5.16.0", {"start": v(-0.15, -1.57) * mm, "end": v(-0.44, -1.74) * mm});
            skLineSegment(sketch, "E5.16.1", {"start": v(-0.15, -1.57) * mm, "end": v(-0.31, -1.3) * mm});
            skLineSegment(sketch, "E5.16.2", {"start": v(-0.44, -1.74) * mm, "end": v(-0.6, -1.47) * mm});
            skLineSegment(sketch, "E5.16.3", {"start": v(-0.31, -1.3) * mm, "end": v(-0.6, -1.47) * mm});
            skLineSegment(sketch, "E5.17.0", {"start": v(-0.48, -1.5) * mm, "end": v(-0.8, -1.6) * mm});
            skLineSegment(sketch, "E5.17.1", {"start": v(-0.48, -1.5) * mm, "end": v(-0.58, -1.2) * mm});
            skLineSegment(sketch, "E5.17.2", {"start": v(-0.8, -1.6) * mm, "end": v(-0.9, -1.3) * mm});
            skLineSegment(sketch, "E5.17.3", {"start": v(-0.58, -1.2) * mm, "end": v(-0.9, -1.3) * mm});
            skLineSegment(sketch, "E5.18.0", {"start": v(-0.8, -1.36) * mm, "end": v(-1.13, -1.4) * mm});
            skLineSegment(sketch, "E5.18.1", {"start": v(-0.8, -1.36) * mm, "end": v(-0.82, -1.04) * mm});
            skLineSegment(sketch, "E5.18.2", {"start": v(-1.13, -1.4) * mm, "end": v(-1.16, -1.08) * mm});
            skLineSegment(sketch, "E5.18.3", {"start": v(-0.82, -1.04) * mm, "end": v(-1.16, -1.08) * mm});
            skLineSegment(sketch, "E5.19.0", {"start": v(-1.06, -1.16) * mm, "end": v(-1.4, -1.12) * mm});
            skLineSegment(sketch, "E5.19.1", {"start": v(-1.06, -1.16) * mm, "end": v(-1.03, -0.84) * mm});
            skLineSegment(sketch, "E5.19.2", {"start": v(-1.4, -1.12) * mm, "end": v(-1.37, -0.8) * mm});
            skLineSegment(sketch, "E5.19.3", {"start": v(-1.03, -0.84) * mm, "end": v(-1.37, -0.8) * mm});
            skLineSegment(sketch, "E5.20.0", {"start": v(-1.29, -0.9) * mm, "end": v(-1.6, -0.8) * mm});
            skLineSegment(sketch, "E5.20.1", {"start": v(-1.29, -0.9) * mm, "end": v(-1.18, -0.6) * mm});
            skLineSegment(sketch, "E5.20.2", {"start": v(-1.6, -0.8) * mm, "end": v(-1.5, -0.5) * mm});
            skLineSegment(sketch, "E5.20.3", {"start": v(-1.18, -0.6) * mm, "end": v(-1.5, -0.5) * mm});
            skLineSegment(sketch, "E5.21.0", {"start": v(-1.45, -0.6) * mm, "end": v(-1.74, -0.43) * mm});
            skLineSegment(sketch, "E5.21.1", {"start": v(-1.45, -0.6) * mm, "end": v(-1.29, -0.34) * mm});
            skLineSegment(sketch, "E5.21.2", {"start": v(-1.74, -0.43) * mm, "end": v(-1.58, -0.16) * mm});
            skLineSegment(sketch, "E5.21.3", {"start": v(-1.29, -0.34) * mm, "end": v(-1.58, -0.16) * mm});
            skLineSegment(sketch, "E5.22.0", {"start": v(-1.55, -0.29) * mm, "end": v(-1.8, -0.05) * mm});
            skLineSegment(sketch, "E5.22.1", {"start": v(-1.55, -0.29) * mm, "end": v(-1.33, -0.05) * mm});
            skLineSegment(sketch, "E5.22.2", {"start": v(-1.8, -0.05) * mm, "end": v(-1.58, 0.18) * mm});
            skLineSegment(sketch, "E5.22.3", {"start": v(-1.33, -0.05) * mm, "end": v(-1.58, 0.18) * mm});
            skLineSegment(sketch, "E5.23.0", {"start": v(-1.57, 0.05) * mm, "end": v(-1.76, 0.33) * mm});
            skLineSegment(sketch, "E5.23.1", {"start": v(-1.57, 0.05) * mm, "end": v(-1.3, 0.23) * mm});
            skLineSegment(sketch, "E5.23.2", {"start": v(-1.76, 0.33) * mm, "end": v(-1.5, 0.51) * mm});
            skLineSegment(sketch, "E5.23.3", {"start": v(-1.3, 0.23) * mm, "end": v(-1.5, 0.51) * mm});
            skLineSegment(sketch, "E5.24.0", {"start": v(-1.52, 0.39) * mm, "end": v(-1.65, 0.7) * mm});
            skLineSegment(sketch, "E5.24.1", {"start": v(-1.52, 0.39) * mm, "end": v(-1.23, 0.5) * mm});
            skLineSegment(sketch, "E5.24.2", {"start": v(-1.65, 0.7) * mm, "end": v(-1.36, 0.82) * mm});
            skLineSegment(sketch, "E5.24.3", {"start": v(-1.23, 0.5) * mm, "end": v(-1.36, 0.82) * mm});
            skLineSegment(sketch, "E5.25.0", {"start": v(-1.4, 0.7) * mm, "end": v(-1.46, 1.04) * mm});
            skLineSegment(sketch, "E5.25.1", {"start": v(-1.4, 0.7) * mm, "end": v(-1.1, 0.76) * mm});
            skLineSegment(sketch, "E5.25.2", {"start": v(-1.46, 1.04) * mm, "end": v(-1.15, 1.1) * mm});
            skLineSegment(sketch, "E5.25.3", {"start": v(-1.1, 0.76) * mm, "end": v(-1.15, 1.1) * mm});
            skLineSegment(sketch, "E5.26.0", {"start": v(-1.22, 0.99) * mm, "end": v(-1.2, 1.33) * mm});
            skLineSegment(sketch, "E5.26.1", {"start": v(-1.22, 0.99) * mm, "end": v(-0.9, 0.98) * mm});
            skLineSegment(sketch, "E5.26.2", {"start": v(-1.2, 1.33) * mm, "end": v(-0.89, 1.32) * mm});
            skLineSegment(sketch, "E5.26.3", {"start": v(-0.9, 0.98) * mm, "end": v(-0.89, 1.32) * mm});
            skLineSegment(sketch, "E5.27.0", {"start": v(-0.98, 1.23) * mm, "end": v(-0.9, 1.56) * mm});
            skLineSegment(sketch, "E5.27.1", {"start": v(-0.98, 1.23) * mm, "end": v(-0.68, 1.15) * mm});
            skLineSegment(sketch, "E5.27.2", {"start": v(-0.9, 1.56) * mm, "end": v(-0.59, 1.48) * mm});
            skLineSegment(sketch, "E5.27.3", {"start": v(-0.68, 1.15) * mm, "end": v(-0.59, 1.48) * mm});
            skLineSegment(sketch, "E5.28.0", {"start": v(-0.7, 1.41) * mm, "end": v(-0.54, 1.71) * mm});
            skLineSegment(sketch, "E5.28.1", {"start": v(-0.7, 1.41) * mm, "end": v(-0.41, 1.27) * mm});
            skLineSegment(sketch, "E5.28.2", {"start": v(-0.54, 1.71) * mm, "end": v(-0.26, 1.57) * mm});
            skLineSegment(sketch, "E5.28.3", {"start": v(-0.41, 1.27) * mm, "end": v(-0.26, 1.57) * mm});
            skLineSegment(sketch, "E5.29.0", {"start": v(-0.38, 1.53) * mm, "end": v(-0.17, 1.8) * mm});
            skLineSegment(sketch, "E5.29.1", {"start": v(-0.38, 1.53) * mm, "end": v(-0.14, 1.33) * mm});
            skLineSegment(sketch, "E5.29.2", {"start": v(-0.17, 1.8) * mm, "end": v(0.08, 1.59) * mm});
            skLineSegment(sketch, "E5.29.3", {"start": v(-0.14, 1.33) * mm, "end": v(0.08, 1.59) * mm});
            skPoint(sketch, "E5.center", {"position": v(0, 0) * mm});
            skLineSegment(sketch, "E5.anchor1", {"start": v(0, 0) * mm, "end": v(-0.07, 1.33) * mm, "construction": true});
            skLineSegment(sketch, "E5.anchor2", {"start": v(0, 0) * mm, "end": v(-0.14, 1.33) * mm, "construction": true});
            skSolve(sketch);
        }
        {
            var Q0;
            {var subQ0=sQuery(id+"F4.wireOp",EDGE,"E5.24.2");var subQ1=sQuery(id+"F4.wireOp",EDGE,"E5.24.0");var subQ2=makeQuery(id+"F4.imprint","INTERSECT",VERTEX,{"derivedFrom":[subQ1,subQ0]});Q0=makeQuery(id+"F4.imprint","IMPRINT",FACE,{"disambiguationData":[TD([[makeQuery(id+"F4.imprint","IMPRINT",EDGE,{"disambiguationData":[TD([[subQ2,1.0]])],"derivedFrom":subQ1}),-1.0]])]});}
            var Q1;
            {var subQ0=sQuery(id+"F4.wireOp",EDGE,"E5.25.2");var subQ1=sQuery(id+"F4.wireOp",EDGE,"E5.25.0");var subQ2=makeQuery(id+"F4.imprint","INTERSECT",VERTEX,{"derivedFrom":[subQ1,subQ0]});Q1=makeQuery(id+"F4.imprint","IMPRINT",FACE,{"disambiguationData":[TD([[makeQuery(id+"F4.imprint","IMPRINT",EDGE,{"disambiguationData":[TD([[subQ2,1.0]])],"derivedFrom":subQ1}),-1.0]])]});}
            var Q2;
            {var subQ0=sQuery(id+"F4.wireOp",EDGE,"E5.26.2");var subQ1=sQuery(id+"F4.wireOp",EDGE,"E5.26.0");var subQ2=makeQuery(id+"F4.imprint","INTERSECT",VERTEX,{"derivedFrom":[subQ1,subQ0]});Q2=makeQuery(id+"F4.imprint","IMPRINT",FACE,{"disambiguationData":[TD([[makeQuery(id+"F4.imprint","IMPRINT",EDGE,{"disambiguationData":[TD([[subQ2,1.0]])],"derivedFrom":subQ1}),-1.0]])]});}
            var Q3;
            {var subQ0=sQuery(id+"F4.wireOp",EDGE,"E5.23.2");var subQ1=sQuery(id+"F4.wireOp",EDGE,"E5.23.0");var subQ2=makeQuery(id+"F4.imprint","INTERSECT",VERTEX,{"derivedFrom":[subQ1,subQ0]});Q3=makeQuery(id+"F4.imprint","IMPRINT",FACE,{"disambiguationData":[TD([[makeQuery(id+"F4.imprint","IMPRINT",EDGE,{"disambiguationData":[TD([[subQ2,1.0]])],"derivedFrom":subQ1}),-1.0]])]});}
            var Q4;
            {var subQ0=sQuery(id+"F4.wireOp",EDGE,"E5.22.2");var subQ1=sQuery(id+"F4.wireOp",EDGE,"E5.22.0");var subQ2=makeQuery(id+"F4.imprint","INTERSECT",VERTEX,{"derivedFrom":[subQ1,subQ0]});Q4=makeQuery(id+"F4.imprint","IMPRINT",FACE,{"disambiguationData":[TD([[makeQuery(id+"F4.imprint","IMPRINT",EDGE,{"disambiguationData":[TD([[subQ2,1.0]])],"derivedFrom":subQ1}),-1.0]])]});}
            var Q5;
            {var subQ0=sQuery(id+"F4.wireOp",EDGE,"E5.21.2");var subQ1=sQuery(id+"F4.wireOp",EDGE,"E5.21.0");var subQ2=makeQuery(id+"F4.imprint","INTERSECT",VERTEX,{"derivedFrom":[subQ1,subQ0]});Q5=makeQuery(id+"F4.imprint","IMPRINT",FACE,{"disambiguationData":[TD([[makeQuery(id+"F4.imprint","IMPRINT",EDGE,{"disambiguationData":[TD([[subQ2,1.0]])],"derivedFrom":subQ1}),-1.0]])]});}
            var Q6;
            {var subQ0=sQuery(id+"F4.wireOp",EDGE,"E5.20.2");var subQ1=sQuery(id+"F4.wireOp",EDGE,"E5.20.0");var subQ2=makeQuery(id+"F4.imprint","INTERSECT",VERTEX,{"derivedFrom":[subQ1,subQ0]});Q6=makeQuery(id+"F4.imprint","IMPRINT",FACE,{"disambiguationData":[TD([[makeQuery(id+"F4.imprint","IMPRINT",EDGE,{"disambiguationData":[TD([[subQ2,1.0]])],"derivedFrom":subQ1}),-1.0]])]});}
            var Q7;
            {var subQ0=sQuery(id+"F4.wireOp",EDGE,"E5.19.2");var subQ1=sQuery(id+"F4.wireOp",EDGE,"E5.19.0");var subQ2=makeQuery(id+"F4.imprint","INTERSECT",VERTEX,{"derivedFrom":[subQ1,subQ0]});Q7=makeQuery(id+"F4.imprint","IMPRINT",FACE,{"disambiguationData":[TD([[makeQuery(id+"F4.imprint","IMPRINT",EDGE,{"disambiguationData":[TD([[subQ2,1.0]])],"derivedFrom":subQ1}),-1.0]])]});}
            var Q8;
            {var subQ0=sQuery(id+"F4.wireOp",EDGE,"E5.18.2");var subQ1=sQuery(id+"F4.wireOp",EDGE,"E5.18.0");var subQ2=makeQuery(id+"F4.imprint","INTERSECT",VERTEX,{"derivedFrom":[subQ1,subQ0]});Q8=makeQuery(id+"F4.imprint","IMPRINT",FACE,{"disambiguationData":[TD([[makeQuery(id+"F4.imprint","IMPRINT",EDGE,{"disambiguationData":[TD([[subQ2,1.0]])],"derivedFrom":subQ1}),-1.0]])]});}
            var Q9;
            {var subQ0=sQuery(id+"F4.wireOp",EDGE,"E5.17.2");var subQ1=sQuery(id+"F4.wireOp",EDGE,"E5.17.0");var subQ2=makeQuery(id+"F4.imprint","INTERSECT",VERTEX,{"derivedFrom":[subQ1,subQ0]});Q9=makeQuery(id+"F4.imprint","IMPRINT",FACE,{"disambiguationData":[TD([[makeQuery(id+"F4.imprint","IMPRINT",EDGE,{"disambiguationData":[TD([[subQ2,1.0]])],"derivedFrom":subQ1}),-1.0]])]});}
            var Q10;
            {var subQ0=sQuery(id+"F4.wireOp",EDGE,"E5.16.2");var subQ1=sQuery(id+"F4.wireOp",EDGE,"E5.16.0");var subQ2=makeQuery(id+"F4.imprint","INTERSECT",VERTEX,{"derivedFrom":[subQ1,subQ0]});Q10=makeQuery(id+"F4.imprint","IMPRINT",FACE,{"disambiguationData":[TD([[makeQuery(id+"F4.imprint","IMPRINT",EDGE,{"disambiguationData":[TD([[subQ2,1.0]])],"derivedFrom":subQ1}),-1.0]])]});}
            var Q11;
            {var subQ0=sQuery(id+"F4.wireOp",EDGE,"E5.15.2");var subQ1=sQuery(id+"F4.wireOp",EDGE,"E5.15.0");var subQ2=makeQuery(id+"F4.imprint","INTERSECT",VERTEX,{"derivedFrom":[subQ1,subQ0]});Q11=makeQuery(id+"F4.imprint","IMPRINT",FACE,{"disambiguationData":[TD([[makeQuery(id+"F4.imprint","IMPRINT",EDGE,{"disambiguationData":[TD([[subQ2,1.0]])],"derivedFrom":subQ1}),-1.0]])]});}
            var Q12;
            {var subQ0=sQuery(id+"F4.wireOp",EDGE,"E5.27.2");var subQ1=sQuery(id+"F4.wireOp",EDGE,"E5.27.0");var subQ2=makeQuery(id+"F4.imprint","INTERSECT",VERTEX,{"derivedFrom":[subQ1,subQ0]});Q12=makeQuery(id+"F4.imprint","IMPRINT",FACE,{"disambiguationData":[TD([[makeQuery(id+"F4.imprint","IMPRINT",EDGE,{"disambiguationData":[TD([[subQ2,1.0]])],"derivedFrom":subQ1}),-1.0]])]});}
            var Q13;
            {var subQ0=sQuery(id+"F4.wireOp",EDGE,"E5.28.2");var subQ1=sQuery(id+"F4.wireOp",EDGE,"E5.28.0");var subQ2=makeQuery(id+"F4.imprint","INTERSECT",VERTEX,{"derivedFrom":[subQ1,subQ0]});Q13=makeQuery(id+"F4.imprint","IMPRINT",FACE,{"disambiguationData":[TD([[makeQuery(id+"F4.imprint","IMPRINT",EDGE,{"disambiguationData":[TD([[subQ2,1.0]])],"derivedFrom":subQ1}),-1.0]])]});}
            var Q14;
            {var subQ0=sQuery(id+"F4.wireOp",EDGE,"E4.left");var subQ1=sQuery(id+"F4.wireOp",EDGE,"E4.top");var subQ2=makeQuery(id+"F4.imprint","INTERSECT",VERTEX,{"derivedFrom":[subQ1,subQ0]});Q14=makeQuery(id+"F4.imprint","IMPRINT",FACE,{"disambiguationData":[TD([[makeQuery(id+"F4.imprint","IMPRINT",EDGE,{"disambiguationData":[TD([[subQ2,-1.0]])],"derivedFrom":subQ1}),-1.0]])]});}
            var Q15;
            {var subQ0=sQuery(id+"F4.wireOp",EDGE,"E5.1.2");var subQ1=sQuery(id+"F4.wireOp",EDGE,"E5.1.0");var subQ2=makeQuery(id+"F4.imprint","INTERSECT",VERTEX,{"derivedFrom":[subQ1,subQ0]});Q15=makeQuery(id+"F4.imprint","IMPRINT",FACE,{"disambiguationData":[TD([[makeQuery(id+"F4.imprint","IMPRINT",EDGE,{"disambiguationData":[TD([[subQ2,1.0]])],"derivedFrom":subQ1}),-1.0]])]});}
            var Q16;
            {var subQ0=sQuery(id+"F4.wireOp",EDGE,"E5.2.2");var subQ1=sQuery(id+"F4.wireOp",EDGE,"E5.2.0");var subQ2=makeQuery(id+"F4.imprint","INTERSECT",VERTEX,{"derivedFrom":[subQ1,subQ0]});Q16=makeQuery(id+"F4.imprint","IMPRINT",FACE,{"disambiguationData":[TD([[makeQuery(id+"F4.imprint","IMPRINT",EDGE,{"disambiguationData":[TD([[subQ2,1.0]])],"derivedFrom":subQ1}),-1.0]])]});}
            var Q17;
            {var subQ0=sQuery(id+"F4.wireOp",EDGE,"E5.3.2");var subQ1=sQuery(id+"F4.wireOp",EDGE,"E5.3.0");var subQ2=makeQuery(id+"F4.imprint","INTERSECT",VERTEX,{"derivedFrom":[subQ1,subQ0]});Q17=makeQuery(id+"F4.imprint","IMPRINT",FACE,{"disambiguationData":[TD([[makeQuery(id+"F4.imprint","IMPRINT",EDGE,{"disambiguationData":[TD([[subQ2,1.0]])],"derivedFrom":subQ1}),-1.0]])]});}
            var Q18;
            {var subQ0=sQuery(id+"F4.wireOp",EDGE,"E5.4.2");var subQ1=sQuery(id+"F4.wireOp",EDGE,"E5.4.0");var subQ2=makeQuery(id+"F4.imprint","INTERSECT",VERTEX,{"derivedFrom":[subQ1,subQ0]});Q18=makeQuery(id+"F4.imprint","IMPRINT",FACE,{"disambiguationData":[TD([[makeQuery(id+"F4.imprint","IMPRINT",EDGE,{"disambiguationData":[TD([[subQ2,1.0]])],"derivedFrom":subQ1}),-1.0]])]});}
            var Q19;
            {var subQ0=sQuery(id+"F4.wireOp",EDGE,"E5.5.2");var subQ1=sQuery(id+"F4.wireOp",EDGE,"E5.5.0");var subQ2=makeQuery(id+"F4.imprint","INTERSECT",VERTEX,{"derivedFrom":[subQ1,subQ0]});Q19=makeQuery(id+"F4.imprint","IMPRINT",FACE,{"disambiguationData":[TD([[makeQuery(id+"F4.imprint","IMPRINT",EDGE,{"disambiguationData":[TD([[subQ2,1.0]])],"derivedFrom":subQ1}),-1.0]])]});}
            var Q20;
            {var subQ0=sQuery(id+"F4.wireOp",EDGE,"E5.6.2");var subQ1=sQuery(id+"F4.wireOp",EDGE,"E5.6.0");var subQ2=makeQuery(id+"F4.imprint","INTERSECT",VERTEX,{"derivedFrom":[subQ1,subQ0]});Q20=makeQuery(id+"F4.imprint","IMPRINT",FACE,{"disambiguationData":[TD([[makeQuery(id+"F4.imprint","IMPRINT",EDGE,{"disambiguationData":[TD([[subQ2,1.0]])],"derivedFrom":subQ1}),-1.0]])]});}
            var Q21;
            {var subQ0=sQuery(id+"F4.wireOp",EDGE,"E5.7.2");var subQ1=sQuery(id+"F4.wireOp",EDGE,"E5.7.0");var subQ2=makeQuery(id+"F4.imprint","INTERSECT",VERTEX,{"derivedFrom":[subQ1,subQ0]});Q21=makeQuery(id+"F4.imprint","IMPRINT",FACE,{"disambiguationData":[TD([[makeQuery(id+"F4.imprint","IMPRINT",EDGE,{"disambiguationData":[TD([[subQ2,1.0]])],"derivedFrom":subQ1}),-1.0]])]});}
            var Q22;
            {var subQ0=sQuery(id+"F4.wireOp",EDGE,"E5.8.2");var subQ1=sQuery(id+"F4.wireOp",EDGE,"E5.8.0");var subQ2=makeQuery(id+"F4.imprint","INTERSECT",VERTEX,{"derivedFrom":[subQ1,subQ0]});Q22=makeQuery(id+"F4.imprint","IMPRINT",FACE,{"disambiguationData":[TD([[makeQuery(id+"F4.imprint","IMPRINT",EDGE,{"disambiguationData":[TD([[subQ2,1.0]])],"derivedFrom":subQ1}),-1.0]])]});}
            var Q23;
            {var subQ0=sQuery(id+"F4.wireOp",EDGE,"E5.9.2");var subQ1=sQuery(id+"F4.wireOp",EDGE,"E5.9.0");var subQ2=makeQuery(id+"F4.imprint","INTERSECT",VERTEX,{"derivedFrom":[subQ1,subQ0]});Q23=makeQuery(id+"F4.imprint","IMPRINT",FACE,{"disambiguationData":[TD([[makeQuery(id+"F4.imprint","IMPRINT",EDGE,{"disambiguationData":[TD([[subQ2,1.0]])],"derivedFrom":subQ1}),-1.0]])]});}
            var Q24;
            {var subQ0=sQuery(id+"F4.wireOp",EDGE,"E5.10.2");var subQ1=sQuery(id+"F4.wireOp",EDGE,"E5.10.0");var subQ2=makeQuery(id+"F4.imprint","INTERSECT",VERTEX,{"derivedFrom":[subQ1,subQ0]});Q24=makeQuery(id+"F4.imprint","IMPRINT",FACE,{"disambiguationData":[TD([[makeQuery(id+"F4.imprint","IMPRINT",EDGE,{"disambiguationData":[TD([[subQ2,1.0]])],"derivedFrom":subQ1}),-1.0]])]});}
            var Q25;
            {var subQ0=sQuery(id+"F4.wireOp",EDGE,"E5.11.2");var subQ1=sQuery(id+"F4.wireOp",EDGE,"E5.11.0");var subQ2=makeQuery(id+"F4.imprint","INTERSECT",VERTEX,{"derivedFrom":[subQ1,subQ0]});Q25=makeQuery(id+"F4.imprint","IMPRINT",FACE,{"disambiguationData":[TD([[makeQuery(id+"F4.imprint","IMPRINT",EDGE,{"disambiguationData":[TD([[subQ2,1.0]])],"derivedFrom":subQ1}),-1.0]])]});}
            var Q26;
            {var subQ0=sQuery(id+"F4.wireOp",EDGE,"E5.12.2");var subQ1=sQuery(id+"F4.wireOp",EDGE,"E5.12.0");var subQ2=makeQuery(id+"F4.imprint","INTERSECT",VERTEX,{"derivedFrom":[subQ1,subQ0]});Q26=makeQuery(id+"F4.imprint","IMPRINT",FACE,{"disambiguationData":[TD([[makeQuery(id+"F4.imprint","IMPRINT",EDGE,{"disambiguationData":[TD([[subQ2,1.0]])],"derivedFrom":subQ1}),-1.0]])]});}
            var Q27;
            {var subQ0=sQuery(id+"F4.wireOp",EDGE,"E5.13.2");var subQ1=sQuery(id+"F4.wireOp",EDGE,"E5.13.0");var subQ2=makeQuery(id+"F4.imprint","INTERSECT",VERTEX,{"derivedFrom":[subQ1,subQ0]});Q27=makeQuery(id+"F4.imprint","IMPRINT",FACE,{"disambiguationData":[TD([[makeQuery(id+"F4.imprint","IMPRINT",EDGE,{"disambiguationData":[TD([[subQ2,1.0]])],"derivedFrom":subQ1}),-1.0]])]});}
            var Q28;
            {var subQ0=sQuery(id+"F4.wireOp",EDGE,"E5.14.2");var subQ1=sQuery(id+"F4.wireOp",EDGE,"E5.14.0");var subQ2=makeQuery(id+"F4.imprint","INTERSECT",VERTEX,{"derivedFrom":[subQ1,subQ0]});Q28=makeQuery(id+"F4.imprint","IMPRINT",FACE,{"disambiguationData":[TD([[makeQuery(id+"F4.imprint","IMPRINT",EDGE,{"disambiguationData":[TD([[subQ2,1.0]])],"derivedFrom":subQ1}),-1.0]])]});}
            extrude(context, id + "F5", {"entities" : qUnion([Q0, Q1, Q2, Q3, Q4, Q5, Q6, Q7, Q8, Q9, Q10, Q11, Q12, Q13, Q14, Q15, Q16, Q17, Q18, Q19, Q20, Q21, Q22, Q23, Q24, Q25, Q26, Q27, Q28]), "operationType" : NewBodyOperationType.ADD, "oppositeDirection" : true, "depth" : 1.02 * mm, "offsetDistance" : 25.4 * mm});
        }
    });
